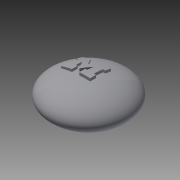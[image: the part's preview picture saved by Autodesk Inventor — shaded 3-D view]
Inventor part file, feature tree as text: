
AUTODESK INVENTOR PART (.ipt)
format: ipt  version: 2015 (Build 190159000, 159)  size: 600,064 bytes
history: native  units: in
note: dims shown in document units (in); Inventor stores cm internally (conversion verified against a paired STEP export)
features: sketch x13, other x11, extrude x7, plane x6, revolve x3, fillet x2
ambient origin geometry x8: Origin, YZ Plane, XZ Plane, XY Plane, X Axis, Y Axis, Z Axis, Center Point
bodies: Body1 (feature_tree)
feature tree (42):
  revolve  "Revolution1"  [1 undecoded]
  other  "Work Axis1"
  sketch  "Sketch3"  dims[d5=1.5in d6=0.75in]
  extrude  "Extrusion3"  Depth=0.75in
  other  "Work Point1"
  plane  "Work Plane1"
  extrude  "Extrusion4"  Depth=0.65in
  extrude  "Extrusion5"  Depth=0.5in TaperAngle=0.0deg
  extrude  "Extrusion6"  Depth=0.01in
  plane  "Work Plane6"
  sketch  "Sketch14"  dims[d49=0.32in d50=0.14in]
  sketch  "Sketch6"  dims[d22=0.2188in d23=0.075in d24=0.0in d25=0.0in d28=0.01in]
  extrude  "Extrusion8"  Depth=1.05in
  revolve  "Revolution6"  [1 undecoded]
  fillet  "Fillet1"  Radius=0.42in
  fillet  "Fillet2"  Radius=0.16in
  sketch  "Sketch15"  dims[d51=0.07in d52=0.04in d53=0.0in]
  other  "Work Point2"
  other  "Work Point3"
  plane  "Work Plane11"
  sketch  "Sketch19"  dims[d54=0.65in d55=0.6545in]
  plane  "Work Plane18"
  extrude  "Extrusion9"  Depth=0.14in
  other  "Work Point4"
  other  "Work Point5"
  other  "Work Point6"
  sketch  "Sketch22"  dims[d61=0.091in d62=0.1in d63=0.0in d64=0.0in]
  plane  "Work Plane20"
  extrude  "Extrusion10"  Depth=0.04in TaperAngle=0.0deg
  other  "Work Point9"
  other  "Work Point10"
  revolve  "Revolution7"  [1 undecoded]
  sketch  "Sketch2"  dims[d3=1.5in d4=0.4375in]
  sketch  "Sketch4"  dims[d8=0.45in d9=0.65in]
  sketch  "Sketch5"  dims[d15=90.0deg d18=0.5in d19=0.0in]
  sketch  "Sketch12"  dims[d42=0.445in d43=1.05in]
  sketch  "Sketch13"  dims[d44=0.345in d45=0.0in d46=0.42in d47=0.42in d48=0.16in]
  plane  "Work Plane10"
  sketch  "Sketch21"  dims[d56=0.6545in]
  other  "Work Point7"
  other  "Work Point8"
  sketch  "Sketch23"  dims[d65=90.0deg d66=0.01in d67=0.47in d68=0.2337in d69=0.2405in d70=0.1202in d75=0.2in d76=0.2405in d77=0.1202in d78=1.05in d79=0.2in d80=0.041in d81=0.2in d82=0.2in d83=0.0in d84=0.0in d85=0.05in d86=0.05in d87=0.3in d88=0.0in d89=0.05in d90=0.05in d91=30.0deg]
note: 3 required parameter values undecoded (feature->parameter linkage not recoverable at this tier; creation-order binding heuristic only, values carry confidence <= 0.55)
